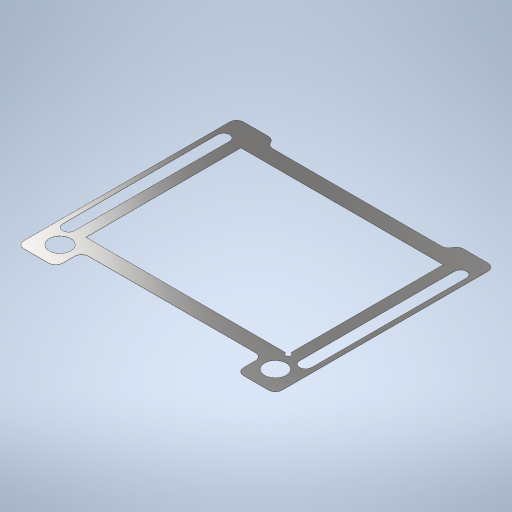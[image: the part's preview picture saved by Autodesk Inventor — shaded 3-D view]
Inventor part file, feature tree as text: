
AUTODESK INVENTOR PART (.ipt)
format: ipt  version: 2023 (Build 270158000, 158)  size: 352,256 bytes
history: native  units: in
note: dims shown in document units (in); Inventor stores cm internally (conversion verified against a paired STEP export)
features: sketch x6, extrude x5, hole x1, fillet x1
ambient origin geometry x8: Origin, YZ Plane, XZ Plane, XY Plane, X Axis, Y Axis, Z Axis, Center Point
bodies: Solid1 (feature_tree)
feature tree (13):
  extrude  "Extrusion1"  Depth=2.75in
  extrude  "Extrusion2"  Depth=0.1378in
  extrude  "Extrusion3"  Depth=1.8in
  hole  "Hole1"  [1 undecoded]
  extrude  "Extrusion4"  Depth=0.45in
  extrude  "Extrusion5"  Depth=0.0787in
  fillet  "Fillet1"  Radius=0.25in
  sketch  "Sketch1"  dims[d0=3.0in d1=2.75in]
  sketch  "Sketch2"  dims[d2=0.002in d3=0.0in d4=0.1378in]
  sketch  "Sketch3"  dims[d5=0.125in d6=1.8in]
  sketch  "Sketch4"  dims[d7=0.0in d8=0.0in d9=0.3in]
  sketch  "Sketch5"  dims[d10=2.1in d11=0.45in]
  sketch  "Sketch6"  dims[d12=0.0in d13=0.0in d14=0.25in d15=0.25in d16=0.25in d17=0.25in d18=0.25in d19=0.25in d20=0.25in d21=0.25in d22=0.251in d23=0.75in d24=0.156in d25=0.073in d26=0.5635in d27=1.0in d28=0.8108in d29=0.2in d30=0.0in d31=0.0in d32=0.0625in d33=1.8in d34=2.35in d35=0.0in d36=0.0in d37=0.0787in d38=0.225in d39=0.075in]
note: 1 required parameter value undecoded (feature->parameter linkage not recoverable at this tier; creation-order binding heuristic only, values carry confidence <= 0.55)
